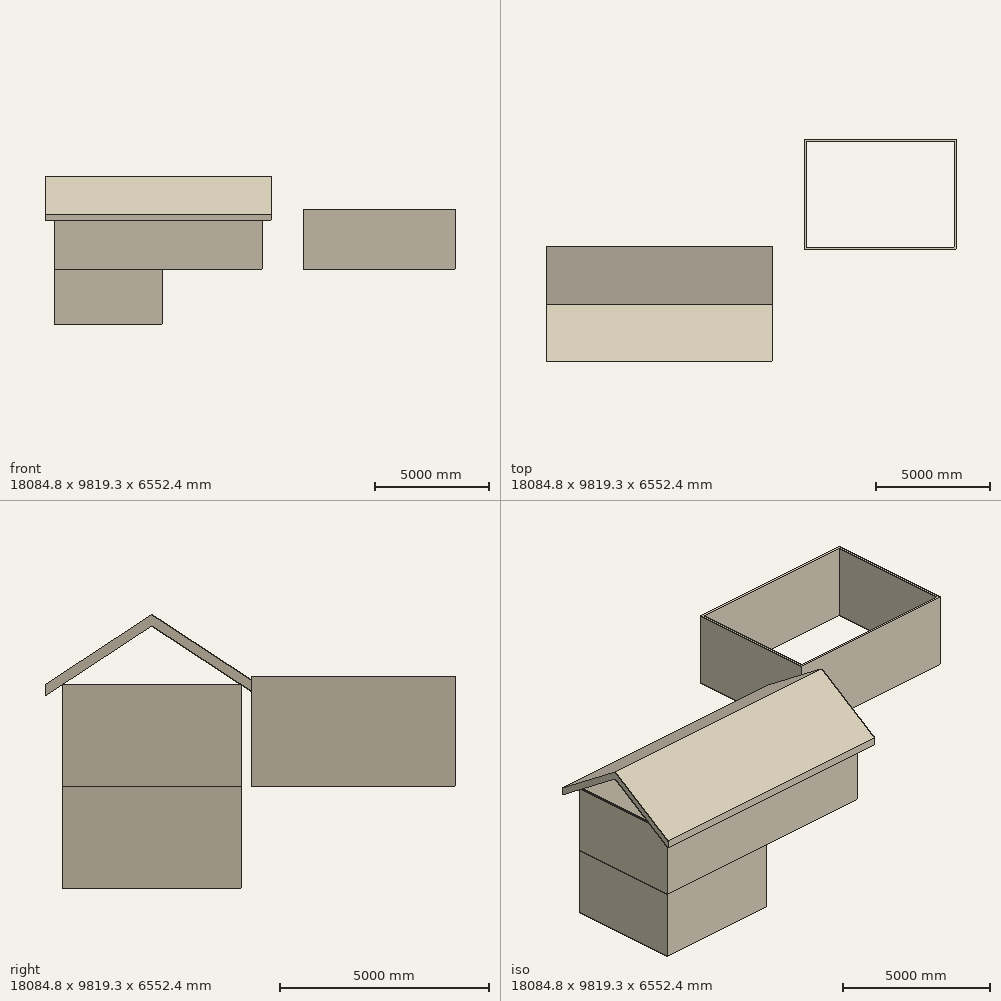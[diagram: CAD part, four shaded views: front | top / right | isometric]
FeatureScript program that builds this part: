
annotation { "Feature Type Name" : "Feature", "Feature Type Description" : "" }
export const myFeature = defineFeature(function(context is Context, id is Id, definition is map)
    precondition{}
    {
        {
            var Q0;
            Q0=qCreatedBy(makeId("Top.planeOp"),FACE);
            var sketch = newSketch(context, id + "F0", { "sketchPlane" : qUnion([Q0])});
            skLineSegment(sketch, "E0.bottom", {"start": v(-22492, 1349.9) * mm, "end": v(15492.17, 1349.9) * mm, "construction": true});
            skLineSegment(sketch, "E0.top", {"start": v(-22492, 13587.62) * mm, "end": v(15492.17, 13587.62) * mm, "construction": true});
            skLineSegment(sketch, "E0.left", {"start": v(-22492, 1349.9) * mm, "end": v(-22492, 13587.62) * mm, "construction": true});
            skLineSegment(sketch, "E0.right", {"start": v(15492.17, 1349.9) * mm, "end": v(15492.17, 13587.62) * mm, "construction": true});
            skLineSegment(sketch, "E1", {"start": v(13084.25, 11667.38) * mm, "end": v(13084.25, 4230.26) * mm});
            skLineSegment(sketch, "E2", {"start": v(13084.25, 4230.26) * mm, "end": v(2903.93, 4230.26) * mm});
            skLineSegment(sketch, "E3", {"start": v(2903.93, 4230.26) * mm, "end": v(2903.93, 7887.86) * mm});
            skLineSegment(sketch, "E4", {"start": v(1136.09, 11667.38) * mm, "end": v(13084.25, 11667.38) * mm});
            skPoint(sketch, "E5.end.orphan", {"position": v(951.76, 167.9) * mm});
            skPoint(sketch, "E6.end.orphan", {"position": v(1224.2, 167.9) * mm});
            skPoint(sketch, "E7.start.orphan", {"position": v(-1915.57, 11667.38) * mm});
            skPoint(sketch, "E8.end.orphan", {"position": v(2903.93, -521.67) * mm});
            skLineSegment(sketch, "E9.bottom", {"start": v(2903.93, 11667.38) * mm, "end": v(-3801.67, 11667.38) * mm});
            skLineSegment(sketch, "E9.top", {"start": v(2903.93, 6790.58) * mm, "end": v(-3801.67, 6790.58) * mm});
            skLineSegment(sketch, "E9.left", {"start": v(2903.93, 11667.38) * mm, "end": v(2903.93, 6790.58) * mm});
            skLineSegment(sketch, "E9.right", {"start": v(-3801.67, 11667.38) * mm, "end": v(-3801.67, 6790.58) * mm});
            skLineSegment(sketch, "E10.bottom", {"start": v(-14774.47, 6531.5) * mm, "end": v(-5630.47, 6531.5) * mm});
            skLineSegment(sketch, "E10.top", {"start": v(-14774.47, 2264.3) * mm, "end": v(-5630.47, 2264.3) * mm});
            skLineSegment(sketch, "E10.left", {"start": v(-14774.47, 6531.5) * mm, "end": v(-14774.47, 2264.3) * mm});
            skLineSegment(sketch, "E10.right", {"start": v(-5630.47, 6531.5) * mm, "end": v(-5630.47, 2264.3) * mm});
            skLineSegment(sketch, "E11.bottom", {"start": v(1989.53, 6790.58) * mm, "end": v(2903.93, 6790.58) * mm});
            skLineSegment(sketch, "E11.top", {"start": v(1989.53, 5876.18) * mm, "end": v(2903.93, 5876.18) * mm});
            skLineSegment(sketch, "E11.left", {"start": v(1989.53, 6790.58) * mm, "end": v(1989.53, 5876.18) * mm});
            skLineSegment(sketch, "E11.right", {"start": v(2903.93, 6790.58) * mm, "end": v(2903.93, 5876.18) * mm});
            skLineSegment(sketch, "E12.bottom", {"start": v(1989.53, 5876.18) * mm, "end": v(465.53, 5876.18) * mm});
            skLineSegment(sketch, "E12.top", {"start": v(1989.53, 6790.58) * mm, "end": v(465.53, 6790.58) * mm});
            skLineSegment(sketch, "E12.left", {"start": v(1989.53, 5876.18) * mm, "end": v(1989.53, 6790.58) * mm});
            skLineSegment(sketch, "E12.right", {"start": v(465.53, 5876.18) * mm, "end": v(465.53, 6790.58) * mm});
            skLineSegment(sketch, "E13", {"start": v(665.53, 6790.58) * mm, "end": v(665.53, 5876.18) * mm});
            skLineSegment(sketch, "E14", {"start": v(665.53, 5876.18) * mm, "end": v(911.26, 5876.18) * mm});
            skLineSegment(sketch, "E15", {"start": v(911.26, 5876.18) * mm, "end": v(911.26, 6790.58) * mm});
            skLineSegment(sketch, "E16", {"start": v(911.26, 6790.58) * mm, "end": v(1227.53, 6790.58) * mm});
            skLineSegment(sketch, "E17", {"start": v(1227.53, 6790.58) * mm, "end": v(1227.53, 5876.18) * mm});
            skLineSegment(sketch, "E18", {"start": v(1227.53, 5876.18) * mm, "end": v(1581.43, 5876.18) * mm});
            skLineSegment(sketch, "E19", {"start": v(1581.43, 5876.18) * mm, "end": v(1581.43, 6790.58) * mm});
            skFitSpline(sketch, "E20", {"points": [v(-5630.47, 6531.5) * mm, v(-1398, 6183.58) * mm, v(465.53, 5551.18) * mm, v(2903.93, 4230.26) * mm], "startDerivative": vector(11816.15, -169.09) * mm, "endDerivative": vector(8171.43, -3283.31) * mm, "construction": true});
            skSolve(sketch);
        }
        {
            var Q0;
            Q0=makeQuery(id+"F0.imprint","IMPRINT",FACE,{"disambiguationData":[TD([[makeQuery(id+"F0.imprint","IMPRINT",EDGE,{"derivedFrom":sQuery(id+"F0.wireOp",EDGE,"E10.bottom")}),-1.0]])]});
            var sketch = newSketch(context, id + "F1", { "sketchPlane" : qUnion([Q0])});
            skLineSegment(sketch, "E21.0.0", {"start": v(-14774.47, 6531.5) * mm, "end": v(-14774.47, 2264.3) * mm});
            skLineSegment(sketch, "E21.0.1", {"start": v(-14774.47, 2264.3) * mm, "end": v(-5630.47, 2264.3) * mm});
            skLineSegment(sketch, "E21.0.2", {"start": v(-5630.47, 2264.3) * mm, "end": v(-5630.47, 6531.5) * mm});
            skLineSegment(sketch, "E21.0.3", {"start": v(-5630.47, 6531.5) * mm, "end": v(-14774.47, 6531.5) * mm});
            skLineSegment(sketch, "E22.0", {"start": v(-14698.27, 6455.3) * mm, "end": v(-14698.27, 2340.5) * mm});
            skLineSegment(sketch, "E22.1", {"start": v(-5706.67, 6455.3) * mm, "end": v(-14698.27, 6455.3) * mm});
            skLineSegment(sketch, "E22.2", {"start": v(-5706.67, 2340.5) * mm, "end": v(-5706.67, 6455.3) * mm});
            skLineSegment(sketch, "E22.3", {"start": v(-14698.27, 2340.5) * mm, "end": v(-5706.67, 2340.5) * mm});
            skSolve(sketch);
        }
        {
            var Q0;
            Q0=makeQuery(id+"F1.imprint","IMPRINT",FACE,{"disambiguationData":[TD([[makeQuery(id+"F1.imprint","IMPRINT",EDGE,{"derivedFrom":sQuery(id+"F1.wireOp",EDGE,"E21.0.0")}),1.0]])]});
            extrude(context, id + "F2", {"entities" : qUnion([Q0]), "depth" : 2438.4 * mm});
        }
        {
            var Q0;
            Q0=makeQuery(id+"F2.opExtrude","SWEPT_FACE",FACE,{"disambiguationData":[OSD([sQuery(id+"F1.wireOp",EDGE,"E21.0.2")])]});
            var sketch = newSketch(context, id + "F3", { "sketchPlane" : qUnion([Q0])});
            skLineSegment(sketch, "E23", {"start": v(4397.9, 2438.4) * mm, "end": v(4397.9, 3840.48) * mm});
            skLineSegment(sketch, "E24", {"start": v(4397.9, 3840.48) * mm, "end": v(2264.3, 2438.4) * mm});
            skLineSegment(sketch, "E25", {"start": v(4397.9, 3840.48) * mm, "end": v(6531.5, 2438.4) * mm});
            skLineSegment(sketch, "E26", {"start": v(2264.3, 2438.4) * mm, "end": v(1848.04, 2164.86) * mm});
            skLineSegment(sketch, "E27", {"start": v(1848.04, 2164.86) * mm, "end": v(1848.04, 2438.4) * mm});
            skLineSegment(sketch, "E28", {"start": v(1848.04, 2438.4) * mm, "end": v(4397.9, 4114.02) * mm});
            skLineSegment(sketch, "E29", {"start": v(4397.9, 4114.02) * mm, "end": v(4397.9, 3840.48) * mm});
            skLineSegment(sketch, "E30", {"start": v(4397.9, 4114.02) * mm, "end": v(6947.76, 2438.4) * mm});
            skLineSegment(sketch, "E31", {"start": v(6531.5, 2438.4) * mm, "end": v(6947.76, 2164.86) * mm});
            skLineSegment(sketch, "E32", {"start": v(6947.76, 2164.86) * mm, "end": v(6947.76, 2438.4) * mm});
            skSolve(sketch);
        }
        {
            var Q0;
            Q0 = qSketchRegion(id + "F3", true);
            extrude(context, id + "F4", {"entities" : qUnion([Q0]), "depth" : 406.4 * mm, "hasSecondDirection" : true, "secondDirectionOppositeDirection" : true, "secondDirectionDepth" : 9550.4 * mm});
        }
        {
            var Q0;
            Q0=makeQuery(id+"F0.imprint","IMPRINT",FACE,{"disambiguationData":[TD([[makeQuery(id+"F0.imprint","IMPRINT",EDGE,{"derivedFrom":sQuery(id+"F0.wireOp",EDGE,"E10.bottom")}),-1.0]])]});
            var sketch = newSketch(context, id + "F5", { "sketchPlane" : qUnion([Q0])});
            skLineSegment(sketch, "E33.0", {"start": v(-14774.47, 2264.3) * mm, "end": v(-10035.52, 2264.3) * mm});
            skLineSegment(sketch, "E34.0", {"start": v(-14698.27, 2340.5) * mm, "end": v(-10124.42, 2340.5) * mm});
            skLineSegment(sketch, "E35.0", {"start": v(-14774.47, 6531.5) * mm, "end": v(-14774.47, 2264.3) * mm});
            skLineSegment(sketch, "E36.0", {"start": v(-14698.27, 6455.3) * mm, "end": v(-14698.27, 2340.5) * mm});
            skLineSegment(sketch, "E37.0", {"start": v(-14774.47, 6531.5) * mm, "end": v(-10035.52, 6531.5) * mm});
            skLineSegment(sketch, "E38", {"start": v(-10035.52, 2264.3) * mm, "end": v(-10035.52, 6531.5) * mm});
            skLineSegment(sketch, "E39", {"start": v(-10035.52, 6531.5) * mm, "end": v(-10124.42, 6531.5) * mm});
            skLineSegment(sketch, "E40", {"start": v(-10124.42, 6455.3) * mm, "end": v(-10124.42, 2340.5) * mm});
            skPoint(sketch, "E41.trimOffspring.end.orphan", {"position": v(-5706.67, 2340.5) * mm});
            skPoint(sketch, "E42.orphan", {"position": v(-5630.47, 2264.3) * mm});
            skLineSegment(sketch, "E43.trimOffspring", {"start": v(-10124.42, 6455.3) * mm, "end": v(-14698.27, 6455.3) * mm});
            skPoint(sketch, "E44.0.start.orphan", {"position": v(-5706.67, 6455.3) * mm});
            skPoint(sketch, "E45.orphan", {"position": v(-5630.47, 6531.5) * mm});
            skSolve(sketch);
        }
        {
            var Q0;
            Q0=makeQuery(id+"F5.imprint","IMPRINT",FACE,{"disambiguationData":[TD([[makeQuery(id+"F5.imprint","IMPRINT",EDGE,{"derivedFrom":sQuery(id+"F5.wireOp",EDGE,"E33.0")}),1.0]])]});
            extrude(context, id + "F6", {"entities" : qUnion([Q0]), "oppositeDirection" : true, "depth" : 2438.4 * mm});
        }
        {
            var Q0;
            {var subQ1=sQuery(id+"F0.wireOp",EDGE,"E9.top");Q0=makeQuery(id+"F0.imprint","IMPRINT",FACE,{"disambiguationData":[TD([[makeQuery(id+"F0.imprint","IMPRINT",EDGE,{"derivedFrom":subQ1}),-1.0]])]});}
            var sketch = newSketch(context, id + "F7", { "sketchPlane" : qUnion([Q0])});
            skLineSegment(sketch, "E46.0", {"start": v(1989.53, 6879.48) * mm, "end": v(2815.03, 6879.48) * mm});
            skLineSegment(sketch, "E46.1", {"start": v(1581.43, 6879.48) * mm, "end": v(1989.53, 6879.48) * mm});
            skLineSegment(sketch, "E46.2", {"start": v(1227.53, 6879.48) * mm, "end": v(1581.43, 6879.48) * mm});
            skLineSegment(sketch, "E46.3", {"start": v(911.26, 6879.48) * mm, "end": v(1227.53, 6879.48) * mm});
            skLineSegment(sketch, "E46.4", {"start": v(665.53, 6879.48) * mm, "end": v(911.26, 6879.48) * mm});
            skLineSegment(sketch, "E46.5", {"start": v(2815.03, 6879.48) * mm, "end": v(2815.03, 7887.86) * mm});
            skLineSegment(sketch, "E46.6", {"start": v(2815.03, 7887.86) * mm, "end": v(2815.03, 11578.48) * mm});
            skLineSegment(sketch, "E46.7", {"start": v(2815.03, 11578.48) * mm, "end": v(-3712.77, 11578.48) * mm});
            skLineSegment(sketch, "E46.8", {"start": v(-3712.77, 11578.48) * mm, "end": v(-3712.77, 6879.48) * mm});
            skLineSegment(sketch, "E46.9", {"start": v(-3712.77, 6879.48) * mm, "end": v(465.53, 6879.48) * mm});
            skLineSegment(sketch, "E46.10", {"start": v(465.53, 6879.48) * mm, "end": v(665.53, 6879.48) * mm});
            skSolve(sketch);
        }
        {
            var Q0;
            Q0=makeQuery(id+"F7.imprint","IMPRINT",FACE,{"disambiguationData":[TD([[makeQuery(id+"F7.imprint","IMPRINT",EDGE,{"derivedFrom":sQuery(id+"F7.wireOp",EDGE,"E46.0")}),-1.0]])]});
            extrude(context, id + "F8", {"entities" : qUnion([Q0]), "depth" : 2641.6 * mm});
        }
    });
